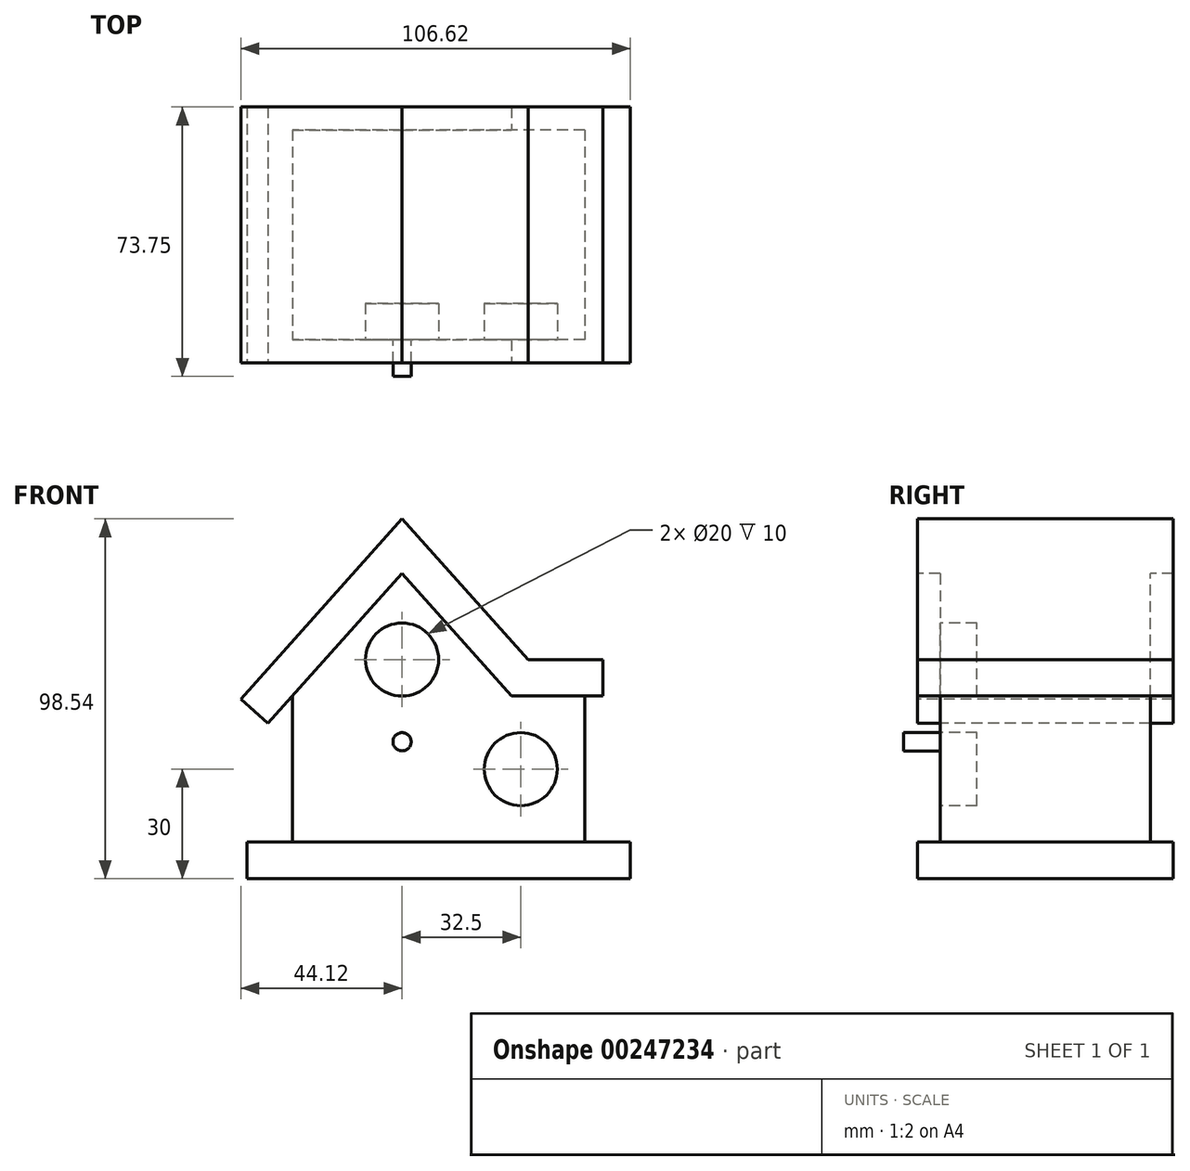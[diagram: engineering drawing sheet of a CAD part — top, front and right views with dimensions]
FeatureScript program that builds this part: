
annotation { "Feature Type Name" : "Feature", "Feature Type Description" : "" }
export const myFeature = defineFeature(function(context is Context, id is Id, definition is map)
    precondition{}
    {
        {
            var Q0;
            Q0=qCreatedBy(makeId("Top.planeOp"),FACE);
            var sketch = newSketch(context, id + "F0", { "sketchPlane" : qUnion([Q0])});
            skLineSegment(sketch, "E0.bottom", {"start": v(52.5, 35) * mm, "end": v(-52.5, 35) * mm});
            skLineSegment(sketch, "E0.top", {"start": v(52.5, -35) * mm, "end": v(-52.5, -35) * mm});
            skLineSegment(sketch, "E0.left", {"start": v(52.5, 35) * mm, "end": v(52.5, -35) * mm});
            skLineSegment(sketch, "E0.right", {"start": v(-52.5, 35) * mm, "end": v(-52.5, -35) * mm});
            skPoint(sketch, "E0.middle", {"position": v(0, 0) * mm});
            skSolve(sketch);
        }
        {
            var Q0;
            Q0 = qSketchRegion(id + "F0", true);
            extrude(context, id + "F1", {"entities" : qUnion([Q0]), "depth" : 10 * mm});
        }
        {
            var Q0;
            Q0=makeQuery(id+"F1.opExtrude","CAP_FACE",FACE,{"disambiguationData":[OSD([sQuery(id+"F0.wireOp",EDGE,"E0.bottom"),sQuery(id+"F0.wireOp",EDGE,"E0.top"),sQuery(id+"F0.wireOp",EDGE,"E0.left"),sQuery(id+"F0.wireOp",EDGE,"E0.right")])],"isStart":false});
            var sketch = newSketch(context, id + "F2", { "sketchPlane" : qUnion([Q0])});
            skLineSegment(sketch, "E1.bottom", {"start": v(40, 28.75) * mm, "end": v(-40, 28.75) * mm});
            skLineSegment(sketch, "E1.top", {"start": v(40, -28.75) * mm, "end": v(-40, -28.75) * mm});
            skLineSegment(sketch, "E1.left", {"start": v(40, 28.75) * mm, "end": v(40, -28.75) * mm});
            skLineSegment(sketch, "E1.right", {"start": v(-40, 28.75) * mm, "end": v(-40, -28.75) * mm});
            skPoint(sketch, "E1.middle", {"position": v(0, 0) * mm});
            skSolve(sketch);
        }
        {
            var Q0;
            Q0=makeQuery(id+"F2.imprint","IMPRINT",FACE,{"disambiguationData":[TD([[makeQuery(id+"F2.imprint","IMPRINT",EDGE,{"derivedFrom":sQuery(id+"F2.wireOp",EDGE,"E1.bottom")}),1.0]])]});
            extrude(context, id + "F3", {"entities" : qUnion([Q0]), "operationType" : NewBodyOperationType.ADD, "depth" : 40 * mm});
        }
        {
            var Q0;
            Q0=makeQuery(id+"F3.opExtrude","SWEPT_FACE",FACE,{"disambiguationData":[OSD([sQuery(id+"F2.wireOp",EDGE,"E1.top")])]});
            var sketch = newSketch(context, id + "F4", { "sketchPlane" : qUnion([Q0])});
            skLineSegment(sketch, "E2", {"start": v(-40, 50) * mm, "end": v(-10, 83.54) * mm});
            skLineSegment(sketch, "E3", {"start": v(-10, 83.54) * mm, "end": v(20, 50) * mm});
            skSolve(sketch);
        }
        {
            var Q0;
            {var subQ0=sQuery(id+"F4.wireOp",EDGE,"E2");Q0=makeQuery(id+"F4.imprint","IMPRINT",FACE,{"disambiguationData":[TD([[makeQuery(id+"F4.imprint","IMPRINT",EDGE,{"derivedFrom":subQ0}),-1.0]])]});}
            extrude(context, id + "F5", {"entities" : qUnion([Q0]), "operationType" : NewBodyOperationType.ADD, "oppositeDirection" : true, "depth" : 57.5 * mm});
        }
        {
            var Q0;
            Q0=makeQuery(id+"F1.opExtrude","SWEPT_FACE",FACE,{"disambiguationData":[OSD([sQuery(id+"F0.wireOp",EDGE,"E0.top")])]});
            var sketch = newSketch(context, id + "F6", { "sketchPlane" : qUnion([Q0])});
            skLineSegment(sketch, "E4", {"start": v(45, 50) * mm, "end": v(45, 60) * mm});
            skLineSegment(sketch, "E5", {"start": v(45, 60) * mm, "end": v(24.47, 60) * mm});
            skLineSegment(sketch, "E6", {"start": v(24.47, 60) * mm, "end": v(-10, 98.54) * mm});
            skLineSegment(sketch, "E7", {"start": v(-10, 98.54) * mm, "end": v(-54.12, 49.21) * mm});
            skLineSegment(sketch, "E8", {"start": v(-54.12, 49.21) * mm, "end": v(-46.67, 42.55) * mm});
            skLineSegment(sketch, "E9.0", {"start": v(-40, 50) * mm, "end": v(-10, 83.54) * mm});
            skPoint(sketch, "E10.0", {"position": v(5, 66.77) * mm});
            skLineSegment(sketch, "E11.0", {"start": v(-10, 83.54) * mm, "end": v(20, 50) * mm});
            skLineSegment(sketch, "E12", {"start": v(-40, 50) * mm, "end": v(-46.67, 42.55) * mm});
            skLineSegment(sketch, "E13", {"start": v(20, 50) * mm, "end": v(45, 50) * mm});
            skSolve(sketch);
        }
        {
            var Q0;
            Q0 = qSketchRegion(id + "F6", true);
            var Q1;
            Q1=makeQuery(id+"F1.opExtrude","SWEPT_FACE",FACE,{"disambiguationData":[OSD([sQuery(id+"F0.wireOp",EDGE,"E0.bottom")])]});
            extrude(context, id + "F7", {"entities" : qUnion([Q0]), "operationType" : NewBodyOperationType.ADD, "endBound" : BoundingType.UP_TO_SURFACE, "oppositeDirection" : true, "endBoundEntityFace" : qUnion([Q1]), "depth" : 70 * mm});
        }
        {
            var Q0;
            {var subQ0=sQuery(id+"F2.wireOp",EDGE,"E1.top");Q0=makeQuery(id+"F5.boolean.opBoolean","MERGE",FACE,{"derivedFrom":[makeQuery(id+"F3.opExtrude","SWEPT_FACE",FACE,{"disambiguationData":[OSD([subQ0])]}),makeQuery(id+"F5.opExtrude","CAP_FACE",FACE,{"disambiguationData":[OSD([subQ0,sQuery(id+"F4.wireOp",EDGE,"E2"),sQuery(id+"F4.wireOp",EDGE,"E3")])],"isStart":true})]});}
            var sketch = newSketch(context, id + "F8", { "sketchPlane" : qUnion([Q0])});
            skCircle(sketch, "E14", {"center": v(-10, 37.5) * mm, "radius": 2.5 * mm});
            skSolve(sketch);
        }
        {
            var Q0;
            Q0=makeQuery(id+"F8.imprint","IMPRINT",FACE,{"disambiguationData":[TD([[makeQuery(id+"F8.imprint","IMPRINT",EDGE,{"derivedFrom":sQuery(id+"F8.wireOp",EDGE,"E14")}),1.0]])]});
            extrude(context, id + "F9", {"entities" : qUnion([Q0]), "operationType" : NewBodyOperationType.ADD, "depth" : 10 * mm});
        }
        {
            var Q0;
            {var subQ0=sQuery(id+"F2.wireOp",EDGE,"E1.top");Q0=makeQuery(id+"F5.boolean.opBoolean","MERGE",FACE,{"derivedFrom":[makeQuery(id+"F3.opExtrude","SWEPT_FACE",FACE,{"disambiguationData":[OSD([subQ0])]}),makeQuery(id+"F5.opExtrude","CAP_FACE",FACE,{"disambiguationData":[OSD([subQ0,sQuery(id+"F4.wireOp",EDGE,"E2"),sQuery(id+"F4.wireOp",EDGE,"E3")])],"isStart":true})]});}
            var sketch = newSketch(context, id + "F10", { "sketchPlane" : qUnion([Q0])});
            skCircle(sketch, "E15", {"center": v(22.5, 30) * mm, "radius": 10 * mm});
            skSolve(sketch);
        }
        {
            var Q0;
            Q0=makeQuery(id+"F10.imprint","IMPRINT",FACE,{"disambiguationData":[TD([[makeQuery(id+"F10.imprint","IMPRINT",EDGE,{"derivedFrom":sQuery(id+"F10.wireOp",EDGE,"E15")}),1.0]])]});
            extrude(context, id + "F11", {"entities" : qUnion([Q0]), "operationType" : NewBodyOperationType.REMOVE, "oppositeDirection" : true, "depth" : 10 * mm});
        }
        {
            var Q0;
            Q0=makeQuery(id+"F10.imprint","IMPRINT",FACE,{"disambiguationData":[TD([[makeQuery(id+"F10.imprint","IMPRINT",EDGE,{"derivedFrom":sQuery(id+"F10.wireOp",EDGE,"E15")}),-1.0]])]});
            var sketch = newSketch(context, id + "F12", { "sketchPlane" : qUnion([Q0])});
            skCircle(sketch, "E16", {"center": v(-10, 60) * mm, "radius": 10 * mm});
            skSolve(sketch);
        }
        {
            var Q0;
            Q0=makeQuery(id+"F12.imprint","IMPRINT",FACE,{"disambiguationData":[TD([[makeQuery(id+"F12.imprint","IMPRINT",EDGE,{"derivedFrom":sQuery(id+"F12.wireOp",EDGE,"E16")}),1.0]])]});
            extrude(context, id + "F13", {"entities" : qUnion([Q0]), "operationType" : NewBodyOperationType.REMOVE, "oppositeDirection" : true, "depth" : 10 * mm});
        }
    });
